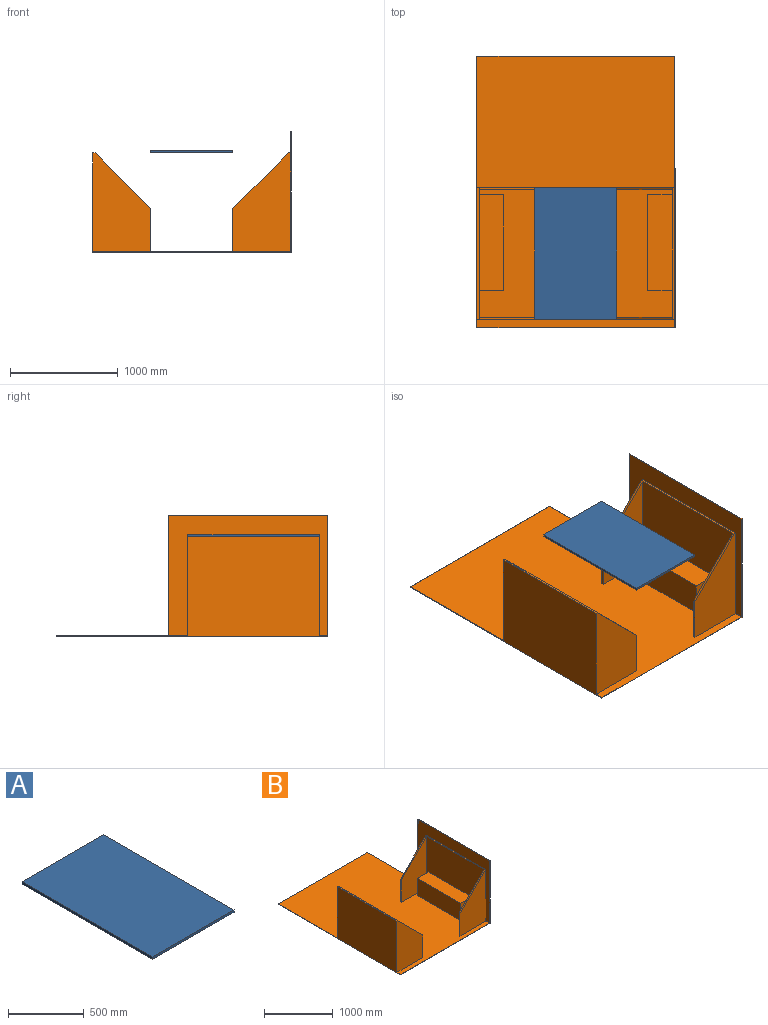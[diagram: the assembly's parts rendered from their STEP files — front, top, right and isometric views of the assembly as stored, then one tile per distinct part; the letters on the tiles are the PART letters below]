
ASSEMBLY  parts=2 mates=3
PART A: 6 faces, bbox 762x1219.2x19.1 mm
  f0: plane 1219.2x19.05mm, normal (1,0,0), area 23225.8mm2, adj f1,f3,f4,f5
  f1: plane 762x19.05mm, normal (0,1,0), area 14516.1mm2, adj f0,f2,f4,f5
  f2: plane 1219.2x19.05mm, normal (-1,0,0), area 23225.8mm2, adj f1,f3,f4,f5
  f3: plane 762x19.05mm, normal (0,-1,0), area 14516.1mm2, adj f0,f2,f4,f5
  f4: plane 1219.2x762mm, normal (0,0,1), area 929030.4mm2, adj f0,f1,f2,f3
  f5: plane 1219.2x762mm, normal (0,0,-1), area 929030.4mm2, adj f0,f1,f2,f3
PART B: 38 faces, bbox 1835.2x2514.6x1117.6 mm
  f0: plane 400.05x19.05mm, normal (-1,0,0), area 7621mm2, adj f2,f4,f12,f36
  f1: plane 400.05x19.05mm, normal (-1,0,0), area 7621mm2, adj f3,f12,f35,f37
  f2: plane 914.4x514.35mm, normal (0,-1,0), area 338043.7mm2, adj f0,f12,f34,f36
  f3: plane 914.4x514.35mm, normal (0,1,0), area 338043.7mm2, adj f1,f12,f34,f37
  f4: plane 914.4x533.4mm, normal (0,1,0), area 355463mm2, adj f0,f5,f6,f12,f36
  f5: plane 1219.2x19.05mm, normal (0,0,1), area 23225.8mm2, adj f4,f6,f34,f35,f36,f37
  f6: plane 1473.2x1111.25mm, normal (-1,0,0), area 522257mm2, adj f4,f5,f12,f14,f18,f19,f35
  f7: plane 304.8x228.6mm, normal (0,1,0), area 69677.3mm2, adj f9,f12,f25,f34
  f8: plane 304.8x228.6mm, normal (0,-1,0), area 69677.3mm2, adj f9,f12,f25,f34
  f9: plane 889x228.6mm, normal (0,0,1), area 203225.4mm2, adj f7,f8,f25,f34
  f10: plane 400.05x19.05mm, normal (1,0,0), area 7621mm2, adj f12,f27,f30,f32
  f11: plane 400.05x19.05mm, normal (1,0,0), area 7621mm2, adj f12,f28,f29,f33
  f12: plane 2514.6x1828.8mm, normal (0,0,1), area 4106604.7mm2, adj f0,f1,f2,f3,f4,f6,f7,f8
  f13: plane 1041.4x6.35mm, normal (1,0,0), area 6612.9mm2, adj f12,f15,f17,f18
  f14: plane 1835.15x1117.6mm, normal (0,-1,0), area 18709.6mm2, adj f6,f12,f16,f17,f19,f20
  f15: plane 1828.8x6.35mm, normal (0,1,0), area 11612.9mm2, adj f12,f13,f16,f17
  f16: plane 2514.6x920.75mm, normal (-1,0,0), area 1130804.2mm2, adj f12,f14,f15,f17,f27,f28,f31
  f17: plane 2514.6x1835.15mm, normal (0,0,-1), area 4608055.3mm2, adj f13,f14,f15,f16,f18,f20
  f18: plane 1117.6x6.35mm, normal (0,1,0), area 7096.8mm2, adj f6,f13,f17,f19,f20
  f19: plane 1473.2x6.35mm, normal (0,0,1), area 9354.8mm2, adj f6,f14,f18,f20
  f20: plane 1473.2x1117.6mm, normal (1,0,0), area 1646448.3mm2, adj f14,f17,f18,f19
  f21: plane 889x304.8mm, normal (1,0,0), area 270967.2mm2, adj f12,f22,f23,f24
  f22: plane 304.8x228.6mm, normal (0,1,0), area 69677.3mm2, adj f12,f21,f24,f26
  f23: plane 304.8x228.6mm, normal (0,-1,0), area 69677.3mm2, adj f12,f21,f24,f26
  f24: plane 889x228.6mm, normal (0,0,1), area 203225.4mm2, adj f21,f22,f23,f26
  f25: plane 889x304.8mm, normal (-1,0,0), area 270967.2mm2, adj f7,f8,f9,f12
  f26: plane 1181.1x914.4mm, normal (1,0,0), area 809030.6mm2, adj f12,f22,f23,f24,f29,f30,f31
  f27: plane 914.4x533.4mm, normal (0,1,0), area 355463mm2, adj f10,f12,f16,f31,f32
  f28: plane 914.4x533.4mm, normal (0,-1,0), area 355463mm2, adj f11,f12,f16,f31,f33
  f29: plane 914.4x514.35mm, normal (0,1,0), area 338043.7mm2, adj f11,f12,f26,f33
  f30: plane 914.4x514.35mm, normal (0,-1,0), area 338043.7mm2, adj f10,f12,f26,f32
  f31: plane 1219.2x19.05mm, normal (0,0,1), area 23225.8mm2, adj f16,f26,f27,f28,f32,f33
  f32: plane 514.35x514.35mm, normal (0.71,0,0.71), area 13857mm2, adj f10,f27,f30,f31
  f33: plane 514.35x514.35mm, normal (0.71,0,0.71), area 13857mm2, adj f11,f28,f29,f31
  f34: plane 1181.1x914.4mm, normal (-1,0,0), area 809030.6mm2, adj f2,f3,f5,f7,f8,f9,f12
  f35: plane 914.4x533.4mm, normal (0,-1,0), area 355463mm2, adj f1,f5,f6,f12,f37
  f36: plane 514.35x514.35mm, normal (-0.71,0,0.71), area 13857mm2, adj f0,f2,f4,f5
  f37: plane 514.35x514.35mm, normal (-0.71,0,0.71), area 13857mm2, adj f1,f3,f5,f35
PLACE A t=(0,-571.5,-183.17)mm
PLACE B t=(0,0,-1103.92)mm
MATE planar A.f3 <-> B.f28  axis (0,-1,0) through (0,-1181.1,-173.65)mm
MATE planar A.f5 <-> B.f31  axis (0,0,-1) through (0,-1181.1,-183.17)mm
MATE planar A.f0 <-> B.f0  axis (1,0,0) through (381,-571.5,-173.65)mm
